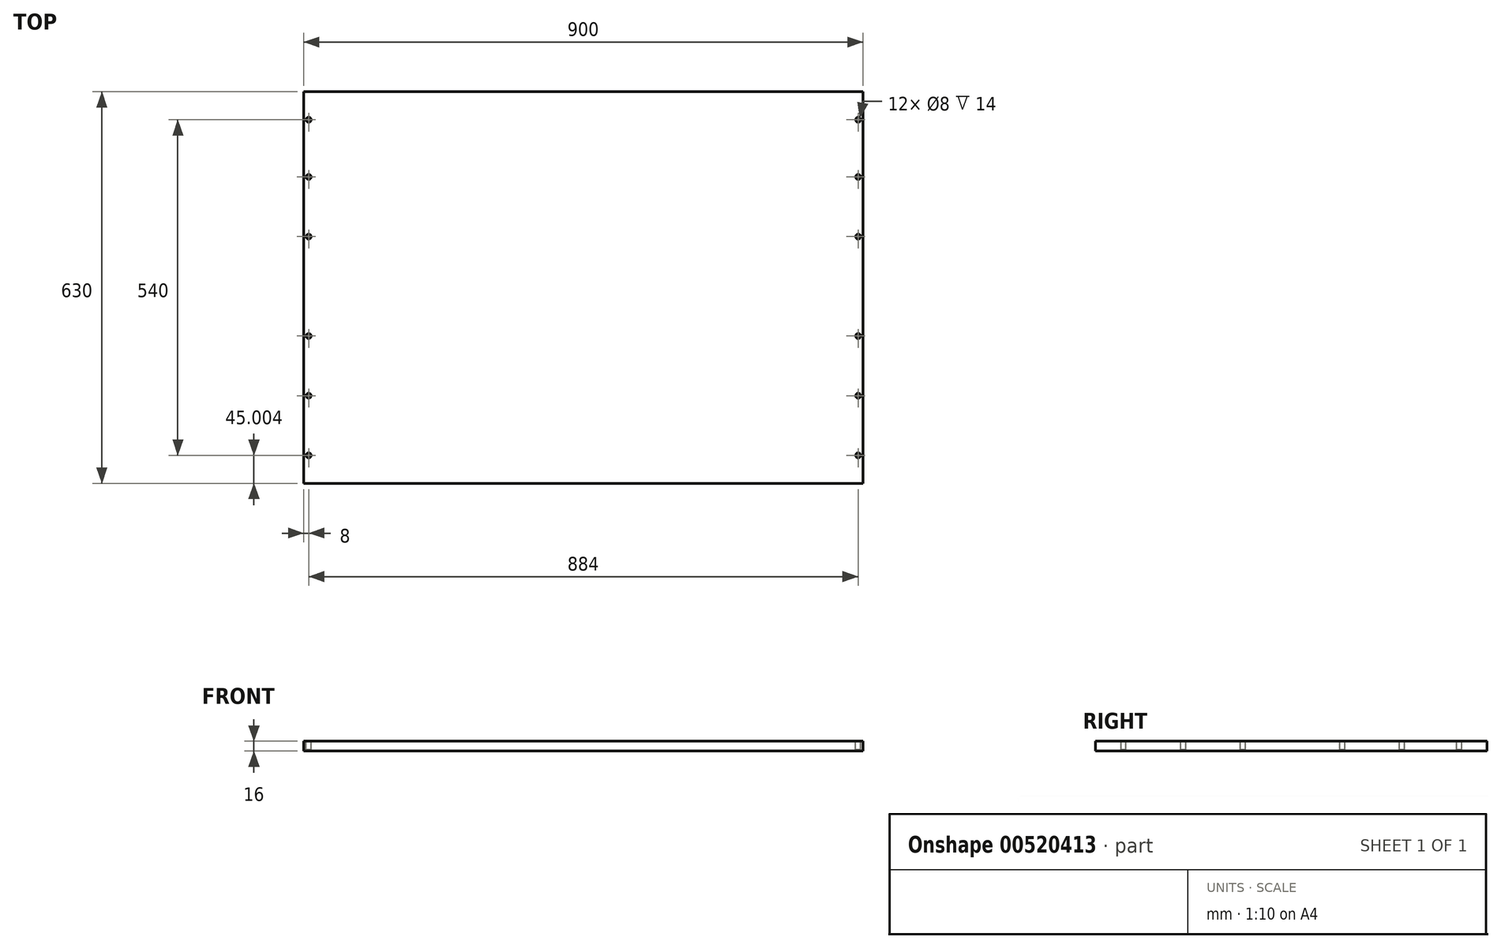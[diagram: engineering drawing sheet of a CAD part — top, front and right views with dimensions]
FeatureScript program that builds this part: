
annotation { "Feature Type Name" : "Feature", "Feature Type Description" : "" }
export const myFeature = defineFeature(function(context is Context, id is Id, definition is map)
    precondition{}
    {
        {
            var Q0;
            Q0=qCreatedBy(makeId("Right.planeOp"),FACE);
            var sketch = newSketch(context, id + "F0", { "sketchPlane" : qUnion([Q0])});
            skLineSegment(sketch, "E0.bottom", {"start": v(-319.14, -32.9) * mm, "end": v(310.86, -32.9) * mm});
            skLineSegment(sketch, "E0.top", {"start": v(-319.14, -48.9) * mm, "end": v(310.86, -48.9) * mm});
            skLineSegment(sketch, "E0.left", {"start": v(-319.14, -32.9) * mm, "end": v(-319.14, -48.9) * mm});
            skLineSegment(sketch, "E0.right", {"start": v(310.86, -32.9) * mm, "end": v(310.86, -48.9) * mm});
            skSolve(sketch);
        }
        {
            var Q0;
            Q0 = qSketchRegion(id + "F0", true);
            extrude(context, id + "F1", {"entities" : qUnion([Q0]), "endBound" : BoundingType.SYMMETRIC, "depth" : 900 * mm, "offsetDistance" : 25 * mm});
        }
        {
            var Q0;
            Q0=makeQuery(id+"F1.opExtrude","SWEPT_FACE",FACE,{"disambiguationData":[OSD([sQuery(id+"F0.wireOp",EDGE,"E0.bottom")])]});
            var sketch = newSketch(context, id + "F2", { "sketchPlane" : qUnion([Q0])});
            skLineSegment(sketch, "E1.0", {"start": v(-450, -319.14) * mm, "end": v(-450, 310.86) * mm, "construction": true});
            skCircle(sketch, "E2", {"center": v(-442, -274.14) * mm, "radius": 4 * mm});
            skLineSegment(sketch, "E3", {"start": v(-442, -274.14) * mm, "end": v(-442, 265.86) * mm, "construction": true});
            skCircle(sketch, "E4", {"center": v(-442, -178.14) * mm, "radius": 4 * mm});
            skCircle(sketch, "E5", {"center": v(-442, -82.14) * mm, "radius": 4 * mm});
            skCircle(sketch, "E6", {"center": v(-442, 77.86) * mm, "radius": 4 * mm});
            skCircle(sketch, "E7", {"center": v(-442, 173.86) * mm, "radius": 4 * mm});
            skCircle(sketch, "E8", {"center": v(-442, 265.86) * mm, "radius": 4 * mm});
            skLineSegment(sketch, "E9", {"start": v(-442, -4.14) * mm, "end": v(-450, -4.14) * mm, "construction": true});
            skCircle(sketch, "E10.MirrorC", {"center": v(442, 265.86) * mm, "radius": 4 * mm});
            skCircle(sketch, "E11.MirrorC", {"center": v(442, -274.14) * mm, "radius": 4 * mm});
            skLineSegment(sketch, "E12.MirrorCS", {"start": v(442, -4.14) * mm, "end": v(450, -4.14) * mm, "construction": true});
            skCircle(sketch, "E13.MirrorC", {"center": v(442, 173.86) * mm, "radius": 4 * mm});
            skCircle(sketch, "E14.MirrorC", {"center": v(442, 77.86) * mm, "radius": 4 * mm});
            skCircle(sketch, "E15.MirrorC", {"center": v(442, -178.14) * mm, "radius": 4 * mm});
            skCircle(sketch, "E16.MirrorC", {"center": v(442, -82.14) * mm, "radius": 4 * mm});
            skLineSegment(sketch, "E17.MirrorCS", {"start": v(450, -319.14) * mm, "end": v(450, 310.86) * mm, "construction": true});
            skLineSegment(sketch, "E18.MirrorCS", {"start": v(442, -274.14) * mm, "end": v(442, 265.86) * mm, "construction": true});
            skSolve(sketch);
        }
        {
            var Q0;
            Q0 = qSketchRegion(id + "F2", true);
            extrude(context, id + "F3", {"entities" : qUnion([Q0]), "operationType" : NewBodyOperationType.REMOVE, "oppositeDirection" : true, "depth" : 14 * mm, "offsetDistance" : 25 * mm});
        }
    });
